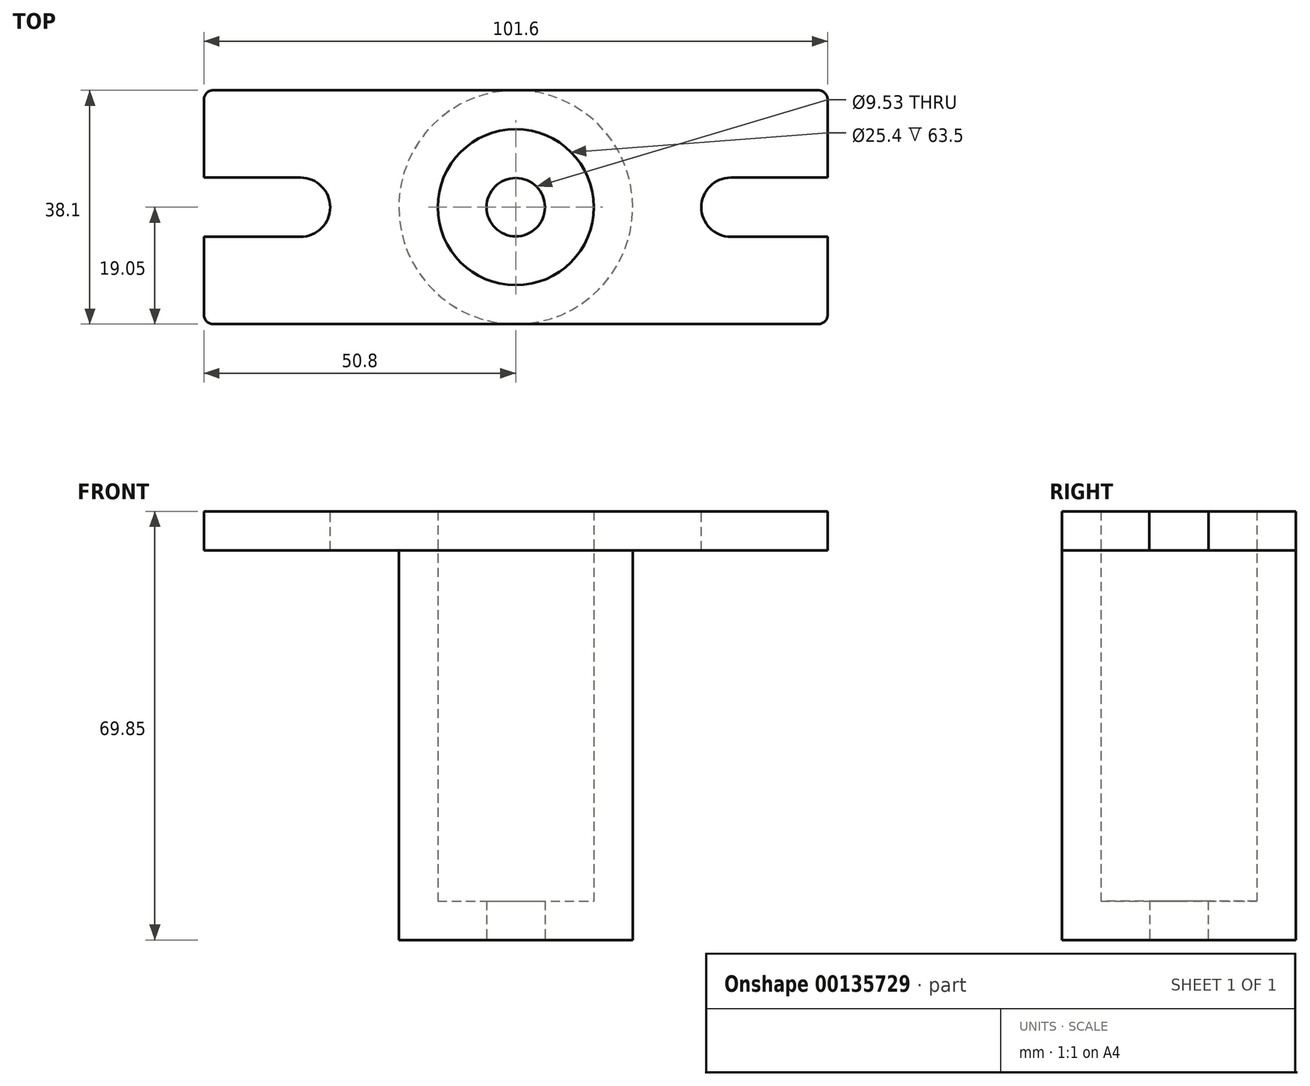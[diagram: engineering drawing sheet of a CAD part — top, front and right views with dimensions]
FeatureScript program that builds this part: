
annotation { "Feature Type Name" : "Feature", "Feature Type Description" : "" }
export const myFeature = defineFeature(function(context is Context, id is Id, definition is map)
    precondition{}
    {
        {
            var Q0;
            Q0=qCreatedBy(makeId("Front.planeOp"),FACE);
            var sketch = newSketch(context, id + "F0", { "sketchPlane" : qUnion([Q0])});
            skLineSegment(sketch, "E0", {"start": v(0, -15.33) * mm, "end": v(0, 67.23) * mm, "construction": true});
            skLineSegment(sketch, "E1", {"start": v(-4.76, 0) * mm, "end": v(-4.76, 6.35) * mm});
            skLineSegment(sketch, "E2", {"start": v(-4.76, 6.35) * mm, "end": v(-12.7, 6.35) * mm});
            skLineSegment(sketch, "E3", {"start": v(-12.7, 6.35) * mm, "end": v(-12.7, 69.85) * mm});
            skLineSegment(sketch, "E4", {"start": v(-12.7, 69.85) * mm, "end": v(-50.8, 69.85) * mm});
            skLineSegment(sketch, "E5", {"start": v(-50.8, 69.85) * mm, "end": v(-50.8, 63.5) * mm});
            skLineSegment(sketch, "E6", {"start": v(-50.8, 63.5) * mm, "end": v(-19.05, 63.5) * mm});
            skLineSegment(sketch, "E7", {"start": v(-19.05, 63.5) * mm, "end": v(-19.05, 0) * mm});
            skLineSegment(sketch, "E8", {"start": v(-19.05, 0) * mm, "end": v(-4.76, 0) * mm});
            skSolve(sketch);
        }
        {
            var Q0;
            Q0=makeQuery(id+"F0.imprint","IMPRINT",FACE,{"disambiguationData":[TD([[makeQuery(id+"F0.imprint","IMPRINT",EDGE,{"derivedFrom":sQuery(id+"F0.wireOp",EDGE,"E1")}),1.0]])]});
            var Q1;
            Q1=sQuery(id+"F0.wireOp",EDGE,"E0");
            revolve(context, id + "F1", {"entities" : qUnion([Q0]), "axis" : qUnion([Q1]), "revolveType" : RevolveType.FULL});
        }
        {
            var Q0;
            Q0=makeQuery(id+"F1.opRevolve","SWEPT_FACE",FACE,{"disambiguationData":[OSD([sQuery(id+"F0.wireOp",EDGE,"E4")])]});
            var sketch = newSketch(context, id + "F2", { "sketchPlane" : qUnion([Q0])});
            skLineSegment(sketch, "E9.bottom", {"start": v(-50.8, 19.05) * mm, "end": v(50.8, 19.05) * mm});
            skLineSegment(sketch, "E9.top", {"start": v(-50.8, -19.05) * mm, "end": v(50.8, -19.05) * mm});
            skLineSegment(sketch, "E9.left", {"start": v(-50.8, 19.05) * mm, "end": v(-50.8, -19.05) * mm});
            skLineSegment(sketch, "E9.right", {"start": v(50.8, 19.05) * mm, "end": v(50.8, -19.05) * mm});
            skLineSegment(sketch, "E10", {"start": v(0, 0) * mm, "end": v(-35.05, 0) * mm, "construction": true});
            skLineSegment(sketch, "E11", {"start": v(-35.05, 0) * mm, "end": v(-50.8, 0) * mm, "construction": true});
            skLineSegment(sketch, "E12", {"start": v(0, 0) * mm, "end": v(35.05, 0) * mm, "construction": true});
            skLineSegment(sketch, "E13", {"start": v(35.05, 0) * mm, "end": v(50.8, 0) * mm, "construction": true});
            skCircle(sketch, "E14", {"center": v(-35.05, 0) * mm, "radius": 4.83 * mm});
            skCircle(sketch, "E15", {"center": v(35.05, 0) * mm, "radius": 4.83 * mm});
            skLineSegment(sketch, "E16", {"start": v(-35.05, 4.83) * mm, "end": v(-50.8, 4.83) * mm});
            skLineSegment(sketch, "E17", {"start": v(-35.05, -4.83) * mm, "end": v(-50.8, -4.83) * mm});
            skLineSegment(sketch, "E18", {"start": v(35.05, 4.83) * mm, "end": v(50.8, 4.83) * mm});
            skLineSegment(sketch, "E19", {"start": v(35.05, -4.83) * mm, "end": v(50.8, -4.83) * mm});
            skSolve(sketch);
        }
        {
            var Q0;
            {var subQ0=sQuery(id+"F2.wireOp",EDGE,"E9.bottom");var subQ1=makeQuery(id+"F1.opRevolve","SWEPT_EDGE",EDGE,{"disambiguationData":[OSD([sQuery(id+"F0.wireOp",EDGE,"E4"),sQuery(id+"F0.wireOp",EDGE,"E5")])]});var subQ2=makeQuery(id+"F2.imprint","INTERSECT",VERTEX,{"disambiguationData":[OD(0.0)],"derivedFrom":[subQ1,subQ0]});Q0=makeQuery(id+"F2.imprint","IMPRINT",FACE,{"disambiguationData":[TD([[makeQuery(id+"F2.imprint","IMPRINT",EDGE,{"disambiguationData":[TD([[subQ2,-1.0]])],"derivedFrom":subQ0}),1.0]])]});}
            var Q1;
            {var subQ0=sQuery(id+"F2.wireOp",EDGE,"E9.top");var subQ1=makeQuery(id+"F1.opRevolve","SWEPT_EDGE",EDGE,{"disambiguationData":[OSD([sQuery(id+"F0.wireOp",EDGE,"E4"),sQuery(id+"F0.wireOp",EDGE,"E5")])]});var subQ2=makeQuery(id+"F2.imprint","INTERSECT",VERTEX,{"disambiguationData":[OD(0.0)],"derivedFrom":[subQ1,subQ0]});Q1=makeQuery(id+"F2.imprint","IMPRINT",FACE,{"disambiguationData":[TD([[makeQuery(id+"F2.imprint","IMPRINT",EDGE,{"disambiguationData":[TD([[subQ2,-1.0]])],"derivedFrom":subQ0}),-1.0]])]});}
            extrude(context, id + "F3", {"entities" : qUnion([Q0, Q1]), "operationType" : NewBodyOperationType.REMOVE, "endBound" : BoundingType.THROUGH_ALL, "oppositeDirection" : true, "depth" : 25.4 * mm});
        }
        {
            var Q0;
            {var subQ0=sQuery(id+"F2.wireOp",EDGE,"E15");var subQ1=makeQuery(id+"F2.imprint","INTERSECT",VERTEX,{"derivedFrom":[subQ0,sQuery(id+"F2.wireOp",EDGE,"E18")]});Q0=makeQuery(id+"F2.imprint","IMPRINT",FACE,{"disambiguationData":[TD([[makeQuery(id+"F2.imprint","IMPRINT",EDGE,{"disambiguationData":[TD([[subQ1,-1.0]])],"derivedFrom":subQ0}),1.0]])]});}
            var Q1;
            {var subQ1=sQuery(id+"F2.wireOp",EDGE,"E15");var subQ6=sQuery(id+"F2.wireOp",EDGE,"E18");var subQ8=makeQuery(id+"F2.imprint","INTERSECT",VERTEX,{"derivedFrom":[subQ1,subQ6]});Q1=makeQuery(id+"F2.imprint","IMPRINT",FACE,{"disambiguationData":[TD([[makeQuery(id+"F2.imprint","IMPRINT",EDGE,{"disambiguationData":[TD([[subQ8,1.0]])],"derivedFrom":subQ1}),-1.0]])]});}
            var Q2;
            {var subQ0=sQuery(id+"F2.wireOp",EDGE,"E14");var subQ1=makeQuery(id+"F2.imprint","INTERSECT",VERTEX,{"derivedFrom":[subQ0,sQuery(id+"F2.wireOp",EDGE,"E16")]});Q2=makeQuery(id+"F2.imprint","IMPRINT",FACE,{"disambiguationData":[TD([[makeQuery(id+"F2.imprint","IMPRINT",EDGE,{"disambiguationData":[TD([[subQ1,-1.0]])],"derivedFrom":subQ0}),1.0]])]});}
            var Q3;
            {var subQ2=sQuery(id+"F2.wireOp",EDGE,"E16");var subQ4=sQuery(id+"F2.wireOp",EDGE,"E14");var subQ5=makeQuery(id+"F2.imprint","INTERSECT",VERTEX,{"derivedFrom":[subQ4,subQ2]});Q3=makeQuery(id+"F2.imprint","IMPRINT",FACE,{"disambiguationData":[TD([[makeQuery(id+"F2.imprint","IMPRINT",EDGE,{"disambiguationData":[TD([[subQ5,-1.0]])],"derivedFrom":subQ4}),-1.0]])]});}
            extrude(context, id + "F4", {"entities" : qUnion([Q0, Q1, Q2, Q3]), "operationType" : NewBodyOperationType.REMOVE, "endBound" : BoundingType.THROUGH_ALL, "oppositeDirection" : true, "depth" : 25.4 * mm});
        }
        {
            var Q0;
            {var subQ0=sQuery(id+"F2.wireOp",EDGE,"E9.left");var subQ1=sQuery(id+"F2.wireOp",EDGE,"E9.bottom");var subQ2=makeQuery(id+"F2.imprint","INTERSECT",VERTEX,{"derivedFrom":[subQ1,subQ0]});Q0=makeQuery(id+"F2.imprint","IMPRINT",FACE,{"disambiguationData":[TD([[makeQuery(id+"F2.imprint","IMPRINT",EDGE,{"disambiguationData":[TD([[subQ2,-1.0]])],"derivedFrom":subQ0}),1.0]])]});}
            var Q1;
            {var subQ0=sQuery(id+"F2.wireOp",EDGE,"E9.left");var subQ1=sQuery(id+"F2.wireOp",EDGE,"E9.top");var subQ2=makeQuery(id+"F2.imprint","INTERSECT",VERTEX,{"derivedFrom":[subQ1,subQ0]});Q1=makeQuery(id+"F2.imprint","IMPRINT",FACE,{"disambiguationData":[TD([[makeQuery(id+"F2.imprint","IMPRINT",EDGE,{"disambiguationData":[TD([[subQ2,1.0]])],"derivedFrom":subQ0}),1.0]])]});}
            var Q2;
            {var subQ0=sQuery(id+"F2.wireOp",EDGE,"E9.right");var subQ1=sQuery(id+"F2.wireOp",EDGE,"E9.bottom");var subQ2=makeQuery(id+"F2.imprint","INTERSECT",VERTEX,{"derivedFrom":[subQ1,subQ0]});Q2=makeQuery(id+"F2.imprint","IMPRINT",FACE,{"disambiguationData":[TD([[makeQuery(id+"F2.imprint","IMPRINT",EDGE,{"disambiguationData":[TD([[subQ2,-1.0]])],"derivedFrom":subQ0}),-1.0]])]});}
            var Q3;
            {var subQ0=sQuery(id+"F2.wireOp",EDGE,"E9.right");var subQ1=sQuery(id+"F2.wireOp",EDGE,"E9.top");var subQ2=makeQuery(id+"F2.imprint","INTERSECT",VERTEX,{"derivedFrom":[subQ1,subQ0]});Q3=makeQuery(id+"F2.imprint","IMPRINT",FACE,{"disambiguationData":[TD([[makeQuery(id+"F2.imprint","IMPRINT",EDGE,{"disambiguationData":[TD([[subQ2,1.0]])],"derivedFrom":subQ0}),-1.0]])]});}
            extrude(context, id + "F5", {"entities" : qUnion([Q0, Q1, Q2, Q3]), "operationType" : NewBodyOperationType.ADD, "oppositeDirection" : true, "depth" : 6.35 * mm});
        }
        {
            var Q0;
            Q0=makeQuery(id+"F5.opExtrude","SWEPT_EDGE",EDGE,{"disambiguationData":[OSD([sQuery(id+"F2.wireOp",EDGE,"E9.top"),sQuery(id+"F2.wireOp",EDGE,"E9.left")])]});
            var Q1;
            Q1=makeQuery(id+"F5.opExtrude","SWEPT_EDGE",EDGE,{"disambiguationData":[OSD([sQuery(id+"F2.wireOp",EDGE,"E9.top"),sQuery(id+"F2.wireOp",EDGE,"E9.right")])]});
            var Q2;
            Q2=makeQuery(id+"F5.opExtrude","SWEPT_EDGE",EDGE,{"disambiguationData":[OSD([sQuery(id+"F2.wireOp",EDGE,"E9.bottom"),sQuery(id+"F2.wireOp",EDGE,"E9.right")])]});
            var Q3;
            Q3=makeQuery(id+"F5.opExtrude","SWEPT_EDGE",EDGE,{"disambiguationData":[OSD([sQuery(id+"F2.wireOp",EDGE,"E9.bottom"),sQuery(id+"F2.wireOp",EDGE,"E9.left")])]});
            fillet(context, id + "F6", {"entities" : qUnion([Q0, Q1, Q2, Q3]), "radius" : 1.52 * mm, "tangentPropagation" : true, "allowEdgeOverflow" : false});
        }
    });
